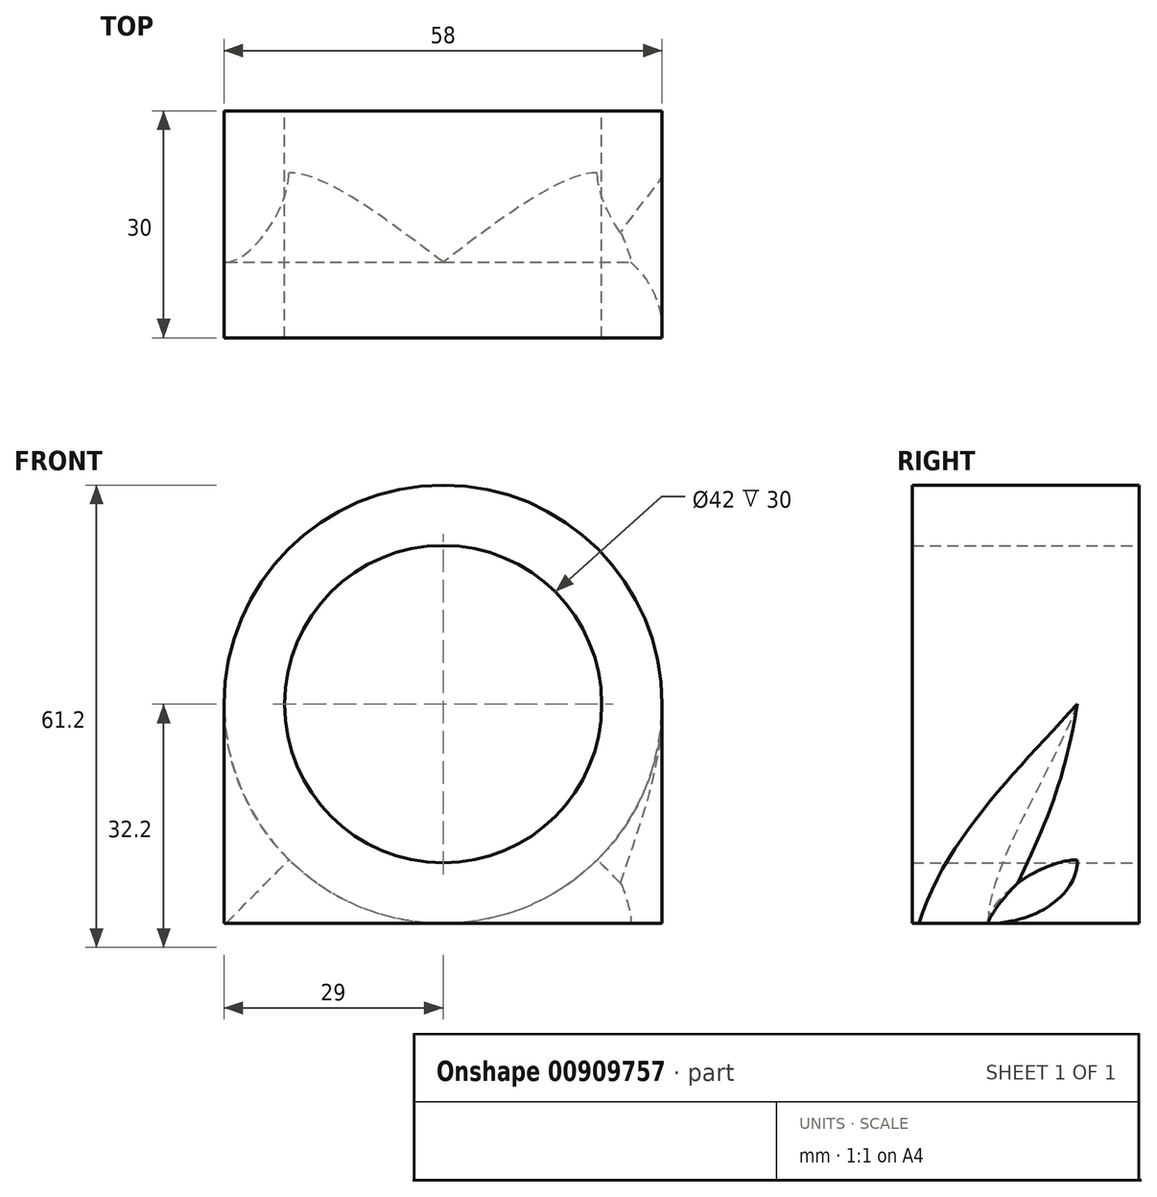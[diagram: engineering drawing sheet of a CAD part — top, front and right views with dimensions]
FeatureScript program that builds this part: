
annotation { "Feature Type Name" : "Feature", "Feature Type Description" : "" }
export const myFeature = defineFeature(function(context is Context, id is Id, definition is map)
    precondition{}
    {
        {
            var Q0;
            Q0=qCreatedBy(makeId("Front.planeOp"),FACE);
            var sketch = newSketch(context, id + "F0", { "sketchPlane" : qUnion([Q0])});
            skCircle(sketch, "E0", {"center": v(0, 0) * mm, "radius": 21 * mm});
            skCircle(sketch, "E1", {"center": v(0, 0) * mm, "radius": 29 * mm});
            skLineSegment(sketch, "E2.bottom", {"start": v(0, 29) * mm, "end": v(0, 29) * mm});
            skLineSegment(sketch, "E2.top", {"start": v(29, -29) * mm, "end": v(-29, -29) * mm});
            skLineSegment(sketch, "E2.left", {"start": v(29, 0) * mm, "end": v(29, -29) * mm});
            skLineSegment(sketch, "E2.right", {"start": v(-29, 0) * mm, "end": v(-29, -29) * mm});
            skPoint(sketch, "E3.visualSharp", {"position": v(-29, 29) * mm});
            skArc(sketch, "E3.filletArc", {"start": v(0, 29) * mm, "mid": v(-20.5, 20.5) * mm, "end": v(-29, 0) * mm});
            skPoint(sketch, "E4.visualSharp", {"position": v(29, 29) * mm});
            skArc(sketch, "E4.filletArc", {"start": v(29, 0) * mm, "mid": v(20.5, 20.5) * mm, "end": v(0, 29) * mm});
            skSolve(sketch);
        }
        {
            var Q0;
            Q0 = qSketchRegion(id + "F0", true);
            extrude(context, id + "F1", {"entities" : qUnion([Q0]), "depth" : 10 * mm, "offsetDistance" : 25 * mm});
        }
        {
            var Q0;
            Q0=makeQuery(id+"F0.imprint","IMPRINT",FACE,{"disambiguationData":[TD([[makeQuery(id+"F0.imprint","IMPRINT",EDGE,{"derivedFrom":sQuery(id+"F0.wireOp",EDGE,"E0")}),-1.0]])]});
            extrude(context, id + "F2", {"entities" : qUnion([Q0]), "operationType" : NewBodyOperationType.ADD, "oppositeDirection" : true, "depth" : 20 * mm, "offsetDistance" : 25 * mm});
        }
        {
            var Q0;
            {var subQ1=sQuery(id+"F0.wireOp",EDGE,"E1");var subQ2=sQuery(id+"F0.wireOp",EDGE,"E2.right");Q0=makeQuery(id+"F2.boolean.opBoolean","SPLIT",EDGE,{"disambiguationData":[TD([makeQuery(id+"F1.opExtrude","SWEPT_FACE",FACE,{"disambiguationData":[OSD([subQ2])]})])],"derivedFrom":makeQuery(id+"F2.opExtrude","CAP_EDGE",EDGE,{"disambiguationData":[OSD([subQ1])],"isStart":true})});}
            fillet(context, id + "F3", {"entities" : qUnion([Q0]), "radius" : 11.83 * mm, "tangentPropagation" : true, "rho" : .3, "crossSection" : FilletCrossSection.CONIC, "allowEdgeOverflow" : false});
        }
        {
            var Q0;
            {var subQ0=sQuery(id+"F0.wireOp",EDGE,"E2.left");var subQ1=makeQuery(id+"F1.opExtrude","SWEPT_FACE",FACE,{"disambiguationData":[OSD([subQ0])]});var subQ3=sQuery(id+"F0.wireOp",EDGE,"E1");Q0=makeQuery(id+"F3.opFillet","BLEND_EDGE",EDGE,{"blendedFrom":[makeQuery(id+"F2.boolean.opBoolean","SPLIT",EDGE,{"disambiguationData":[TD([subQ1])],"derivedFrom":makeQuery(id+"F2.opExtrude","CAP_EDGE",EDGE,{"disambiguationData":[OSD([subQ3])],"isStart":true})}),subQ1],"blendedInto":[subQ1]});}
            var Q1;
            {var subQ0=sQuery(id+"F0.wireOp",EDGE,"E2.right");var subQ1=makeQuery(id+"F1.opExtrude","SWEPT_FACE",FACE,{"disambiguationData":[OSD([subQ0])]});var subQ3=sQuery(id+"F0.wireOp",EDGE,"E1");Q1=makeQuery(id+"F3.opFillet","BLEND_EDGE",EDGE,{"blendedFrom":[makeQuery(id+"F2.boolean.opBoolean","SPLIT",EDGE,{"disambiguationData":[TD([subQ1])],"derivedFrom":makeQuery(id+"F2.opExtrude","CAP_EDGE",EDGE,{"disambiguationData":[OSD([subQ3])],"isStart":true})}),subQ1],"blendedInto":[subQ1]});}
            fillet(context, id + "F4", {"entities" : qUnion([Q0, Q1]), "radius" : 10.88 * mm, "tangentPropagation" : true, "allowEdgeOverflow" : false});
        }
    });
